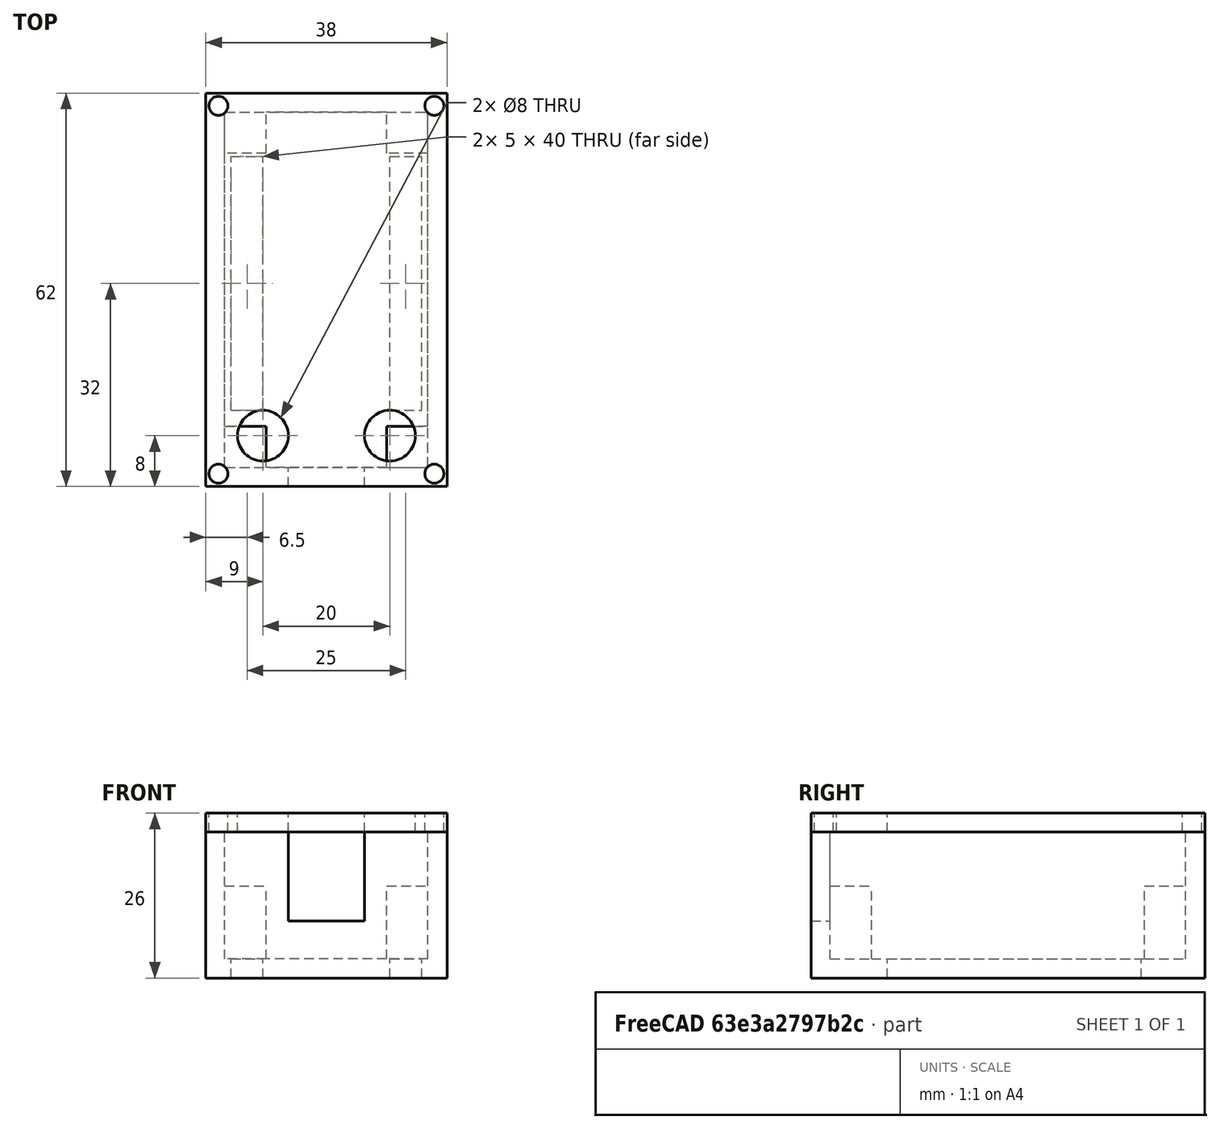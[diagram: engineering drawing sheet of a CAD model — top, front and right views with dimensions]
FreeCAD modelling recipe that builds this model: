
FCSTD DOCUMENT  (FreeCAD 0.16R6706 (Git))
Label: copia seguridad 1
License: All rights reserved
LicenseURL: http://en.wikipedia.org/wiki/All_rights_reserved
objects: Part::Box×11, Part::MultiFuse×6, Part::Cylinder×6, Part::Cut×5
note: 28 computed .brp shape members not serialized (recipe doc carries the construction recipe); baked Part::Feature solids carry a one-line shape summary decoded from their .brp

FEATURE [Part::Box] Box  label="1"
  Height = 23
  Length = 38
  Width = 62
FEATURE [Part::Box] Box001  label="2"
  Height = 23
  Length = 32
  Placement = pos=(3,3,0) rot=(0,0,1;0rad)
  Width = 56
FEATURE [Part::Box] Box002  label="carcasa fondo"
  Height = 3
  Length = 38
  Width = 62
FEATURE [Part::Box] Box003  label="tapa2"
  Height = 3
  Length = 38
  Placement = pos=(0,0,23) rot=(0,0,1;0rad)
  Width = 62
FEATURE [Part::Cut] Cut  label="carcasa laterales"
  Base = -> Box
  Tool = -> Box001
FEATURE [Part::MultiFuse] Fusion  label="carcasa_2"
  Shapes = -> [Box002,Cut]
FEATURE [Part::Box] Box004  label="soporte 1"
  Height = 14.5
  Length = 6.5
  Placement = pos=(3,3,0) rot=(0,0,1;0rad)
  Width = 6.5
FEATURE [Part::Box] Box005  label="soporte 2"
  Height = 14.5
  Length = 6.5
  Placement = pos=(28.5,3,0) rot=(0,0,1;0rad)
  Width = 6.5
FEATURE [Part::Box] Box006  label="soporte 3"
  Height = 14.5
  Length = 6.5
  Placement = pos=(3,52.5,0) rot=(0,0,1;0rad)
  Width = 6.5
FEATURE [Part::Box] Box007  label="soporte 4"
  Height = 14.5
  Length = 6.5
  Placement = pos=(28.5,52.5,0) rot=(0,0,1;0rad)
  Width = 6.5
FEATURE [Part::MultiFuse] Fusion001  label="soportes"
  Shapes = -> [Box004,Box005,Box006,Box007]
FEATURE [Part::MultiFuse] Fusion002  label="01"
  Shapes = -> [Fusion,Fusion001]
FEATURE [Part::Box] Box008  label="rendija 1"
  Height = 3
  Length = 5
  Placement = pos=(4,12,0) rot=(0,0,1;0rad)
  Width = 40
FEATURE [Part::Box] Box009  label="rendija 2"
  Height = 3
  Length = 5
  Placement = pos=(29,12,0) rot=(0,0,1;0rad)
  Width = 40
FEATURE [Part::MultiFuse] Fusion003  label="rendijas"
  Shapes = -> [Box008,Box009]
FEATURE [Part::Cut] Cut001  label="02"
  Base = -> Fusion002
  Tool = -> Fusion003
FEATURE [Part::Box] Box010  label="03"
  Height = 14
  Length = 12
  Placement = pos=(13,0,9) rot=(0,0,1;0rad)
  Width = 3
FEATURE [Part::Cut] Cut002  label="carcasa"
  Base = -> Cut001
  Tool = -> Box010
FEATURE [Part::Cylinder] Cylinder  label="switch1"
  Angle = 360
  Height = 10
  Placement = pos=(9,8,23) rot=(0,0,1;0rad)
  Radius = 4
FEATURE [Part::Cylinder] Cylinder001  label="switch2"
  Angle = 360
  Height = 10
  Placement = pos=(29,8,23) rot=(0,0,1;0rad)
  Radius = 4
FEATURE [Part::MultiFuse] Fusion004  label="switches"
  Shapes = -> [Cylinder,Cylinder001]
FEATURE [Part::Cut] Cut003  label="tapa3"
  Base = -> Box003
  Tool = -> Fusion004
FEATURE [Part::Cylinder] Cylinder002  label="tornillo1"
  Angle = 360
  Height = 3
  Placement = pos=(2,2,23) rot=(0,0,1;0rad)
  Radius = 1.5
FEATURE [Part::Cylinder] Cylinder003  label="tornillo2"
  Angle = 360
  Height = 3
  Placement = pos=(36,2,23) rot=(0,0,1;0rad)
  Radius = 1.5
FEATURE [Part::Cylinder] Cylinder004  label="tornillo3"
  Angle = 360
  Height = 3
  Placement = pos=(2,60,23) rot=(0,0,1;0rad)
  Radius = 1.5
FEATURE [Part::Cylinder] Cylinder005  label="tornillo4"
  Angle = 360
  Height = 3
  Placement = pos=(36,60,23) rot=(0,0,1;0rad)
  Radius = 1.5
FEATURE [Part::MultiFuse] Fusion005  label="tornillos"
  Shapes = -> [Cylinder002,Cylinder003,Cylinder004,Cylinder005]
FEATURE [Part::Cut] Cut004  label="tapa"
  Base = -> Cut003
  Tool = -> Fusion005
